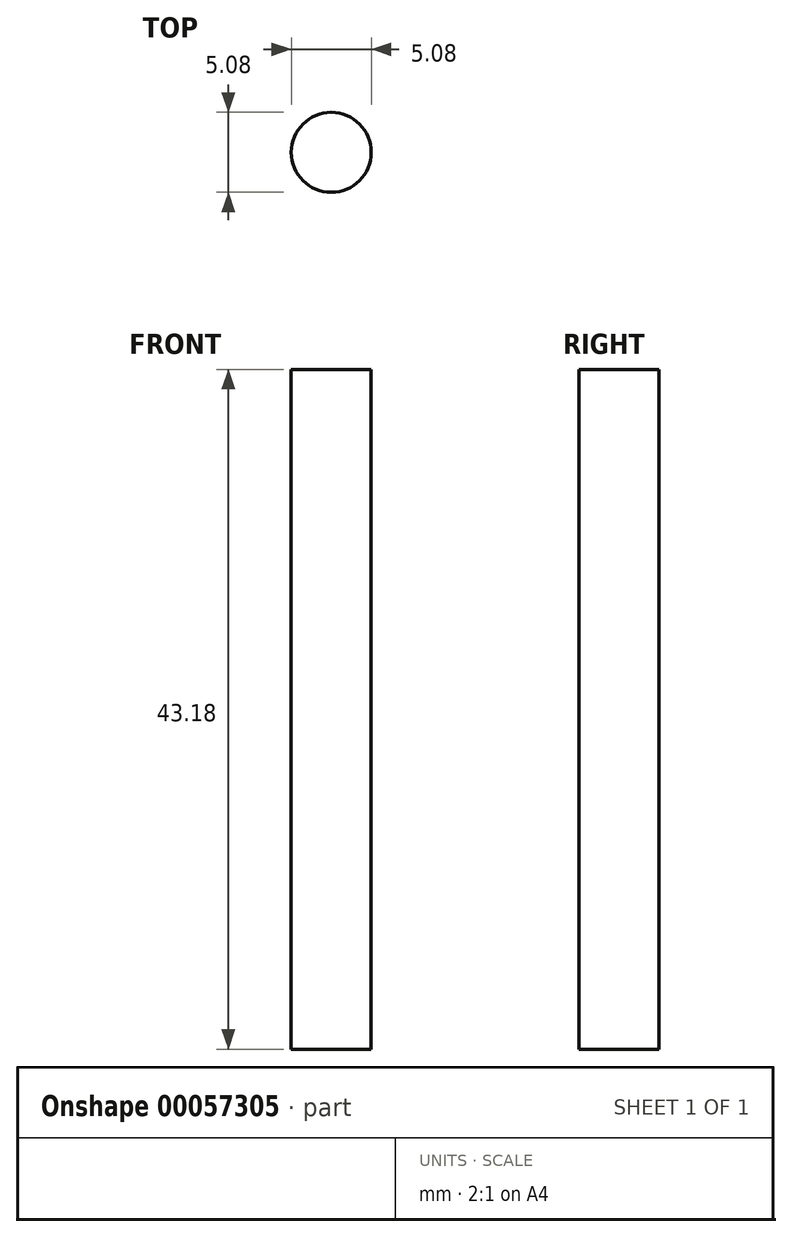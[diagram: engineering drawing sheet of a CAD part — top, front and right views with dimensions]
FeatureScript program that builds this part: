
annotation { "Feature Type Name" : "Feature", "Feature Type Description" : "" }
export const myFeature = defineFeature(function(context is Context, id is Id, definition is map)
    precondition{}
    {
        {
            var Q0;
            Q0=qCreatedBy(makeId("Top.planeOp"),FACE);
            var sketch = newSketch(context, id + "F0", { "sketchPlane" : qUnion([Q0])});
            skCircle(sketch, "E0", {"center": v(-28.34, 36.99) * mm, "radius": 2.54 * mm});
            skSolve(sketch);
        }
        {
            var Q0;
            Q0 = qSketchRegion(id + "F0", true);
            extrude(context, id + "F1", {"entities" : qUnion([Q0]), "depth" : 43.18 * mm});
        }
    });
